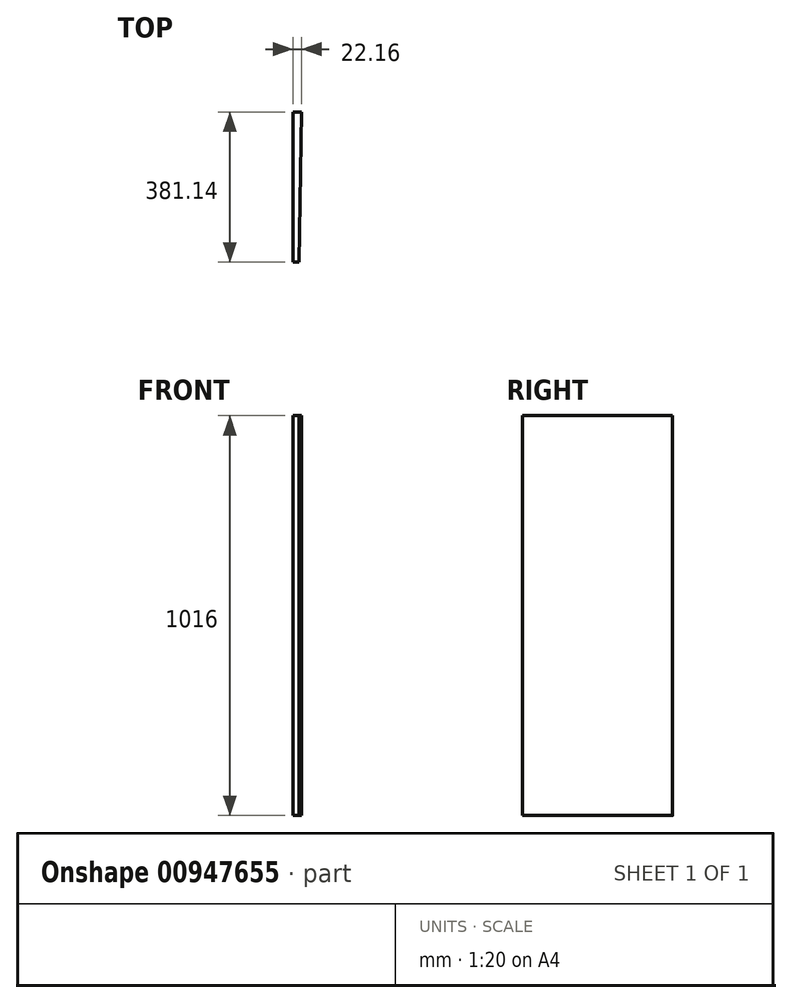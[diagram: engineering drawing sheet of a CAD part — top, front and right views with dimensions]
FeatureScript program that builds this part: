
annotation { "Feature Type Name" : "Feature", "Feature Type Description" : "" }
export const myFeature = defineFeature(function(context is Context, id is Id, definition is map)
    precondition{}
    {
        {
            var Q0;
            Q0=qCreatedBy(makeId("Top.planeOp"),FACE);
            var sketch = newSketch(context, id + "F0", { "sketchPlane" : qUnion([Q0])});
            skCircle(sketch, "E0", {"center": v(0, 0) * mm, "radius": 1270 * mm});
            skCircle(sketch, "E1", {"center": v(0, 0) * mm, "radius": 889 * mm});
            skSolve(sketch);
        }
        {
            var Q0;
            Q0=qCreatedBy(makeId("Top.planeOp"),FACE);
            var sketch = newSketch(context, id + "F1", { "sketchPlane" : qUnion([Q0])});
            skLineSegment(sketch, "E2", {"start": v(0, 1270) * mm, "end": v(0, 889) * mm});
            skArc(sketch, "E3.0", {"start": v(22.16, 1269.8) * mm, "mid": v(11.08, 1269.95) * mm, "end": v(0, 1270) * mm});
            skArc(sketch, "E4.0", {"start": v(15.52, 888.86) * mm, "mid": v(7.76, 888.97) * mm, "end": v(0, 889) * mm});
            skLineSegment(sketch, "E5", {"start": v(15.52, 888.86) * mm, "end": v(22.16, 1269.8) * mm});
            skSolve(sketch);
        }
        {
            var Q0;
            Q0 = qSketchRegion(id + "F1", true);
            extrude(context, id + "F2", {"entities" : qUnion([Q0]), "depth" : 1016 * mm, "offsetDistance" : 25.4 * mm});
        }
    });
